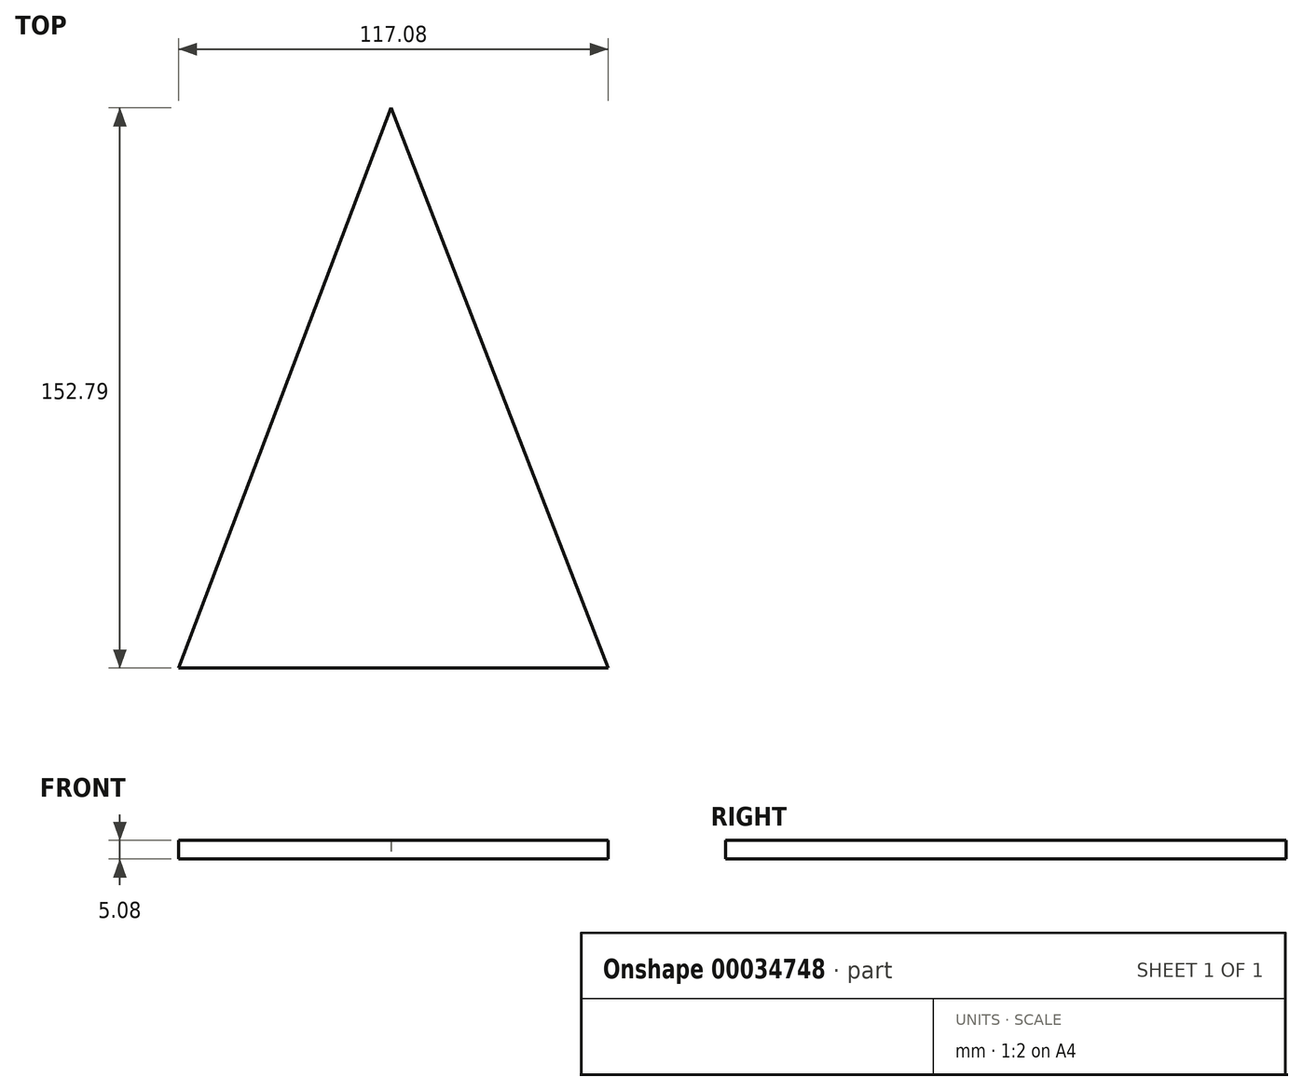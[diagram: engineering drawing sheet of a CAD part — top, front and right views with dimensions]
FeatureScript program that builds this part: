
annotation { "Feature Type Name" : "Feature", "Feature Type Description" : "" }
export const myFeature = defineFeature(function(context is Context, id is Id, definition is map)
    precondition{}
    {
        {
            var Q0;
            Q0=qCreatedBy(makeId("Top.planeOp"),FACE);
            var sketch = newSketch(context, id + "F0", { "sketchPlane" : qUnion([Q0])});
            skLineSegment(sketch, "E0", {"start": v(0, 76.52) * mm, "end": v(-57.92, -76.27) * mm});
            skLineSegment(sketch, "E1", {"start": v(0, 76.52) * mm, "end": v(59.16, -76.27) * mm});
            skLineSegment(sketch, "E2", {"start": v(-57.92, -76.27) * mm, "end": v(59.16, -76.27) * mm});
            skSolve(sketch);
        }
        {
            var Q0;
            Q0=makeQuery(id+"F0.imprint","IMPRINT",FACE,{"disambiguationData":[TD([[makeQuery(id+"F0.imprint","IMPRINT",EDGE,{"derivedFrom":sQuery(id+"F0.wireOp",EDGE,"E0")}),1.0]])]});
            extrude(context, id + "F1", {"entities" : qUnion([Q0]), "depth" : 5.08 * mm});
        }
    });
